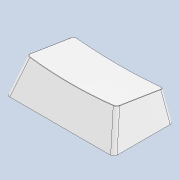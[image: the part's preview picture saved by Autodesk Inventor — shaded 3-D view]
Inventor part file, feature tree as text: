
AUTODESK INVENTOR PART (.ipt)
format: ipt  version: 2021 (Build 250183000, 183)  size: 239,104 bytes
history: native  units: in
note: dims shown in document units (in); Inventor stores cm internally (conversion verified against a paired STEP export)
features: chamfer x1
ambient origin geometry x8: Origin, YZ Plane, XZ Plane, XY Plane, X Axis, Y Axis, Z Axis, Center Point
bodies: Solid1 (feature_tree)
feature tree (1):
  chamfer  "Chamfer1"  [1 undecoded]
note: 1 required parameter value undecoded (feature->parameter linkage not recoverable at this tier; creation-order binding heuristic only, values carry confidence <= 0.55)
